# Revit family: Kingsway Shower Doorset_v3.0 (29.07.23)
name_source: partatom
category: Doors
units: mm (PartAtom-declared; Revit-internal decimal feet)

## family parameters
Always vertical = Yes
Cut with Voids When Loaded = No
Host = Wall
OmniClass Number = 23.30.10.00
OmniClass Title = Doors
Room Calculation Point = No
Shared = No

## types (1)
- 1100 x 2100
    Action = Double
    Analytic Construction = <None>
    Architrave Material = Hardwood or softwood.
    Bead Material = None.
    Configuration = Single Leaf
    Description = The next generation of anti-ligature en-suite doors - high impact moisture proof door leaf with double action full height hinge mechanism and anti-trap rubber fin to the frame closing side.
    Door - Leaf Finish Notes = For full range of available finishes and colours, contact Kingsway Group.
    Door Leaf Height = 1500 mm  [stored 4.92126 ft]
    Door Leaf Width = 845 mm
    Fire Rating = NFR
    Frame Thickness = 35 mm  [stored 0.114829 ft]
    Function = Interior
    Height = 2100 mm
    HeightOfCloserStrip = 1500 mm  [stored 4.92126 ft]
    HeightOfSwingHinge = 1808 mm
    KGFlexibleCloserStrip = Yes
    KGShowerDoorHinge = Yes
    Keynote = L20
    Leaf Core Structure = Rot proof door core for longevity and durability.
    Lipping Material = None.
    Manufacturer = Kingsway Group
    Model = Shower Doorset
    Rough Height = 2100 mm
    Rough Width = 1100 mm
    Telephone = 01322 610 470
    Thickness = 10 mm  [stored 0.0328084 ft]
    URL = https://www.kingswaygroupglobal.com
    Version = 3.0 (29.07.23)
    Vision Panel = None.
    Wall Closure = Neither
    Width = 1100 mm

note: [stored X ft] marks values corroborated as IEEE doubles in the binary element streams (Revit-internal decimal feet)

## geometry (parser evidence)
native form markers: Sweep x13
no freeform markers — native parametric forms only
